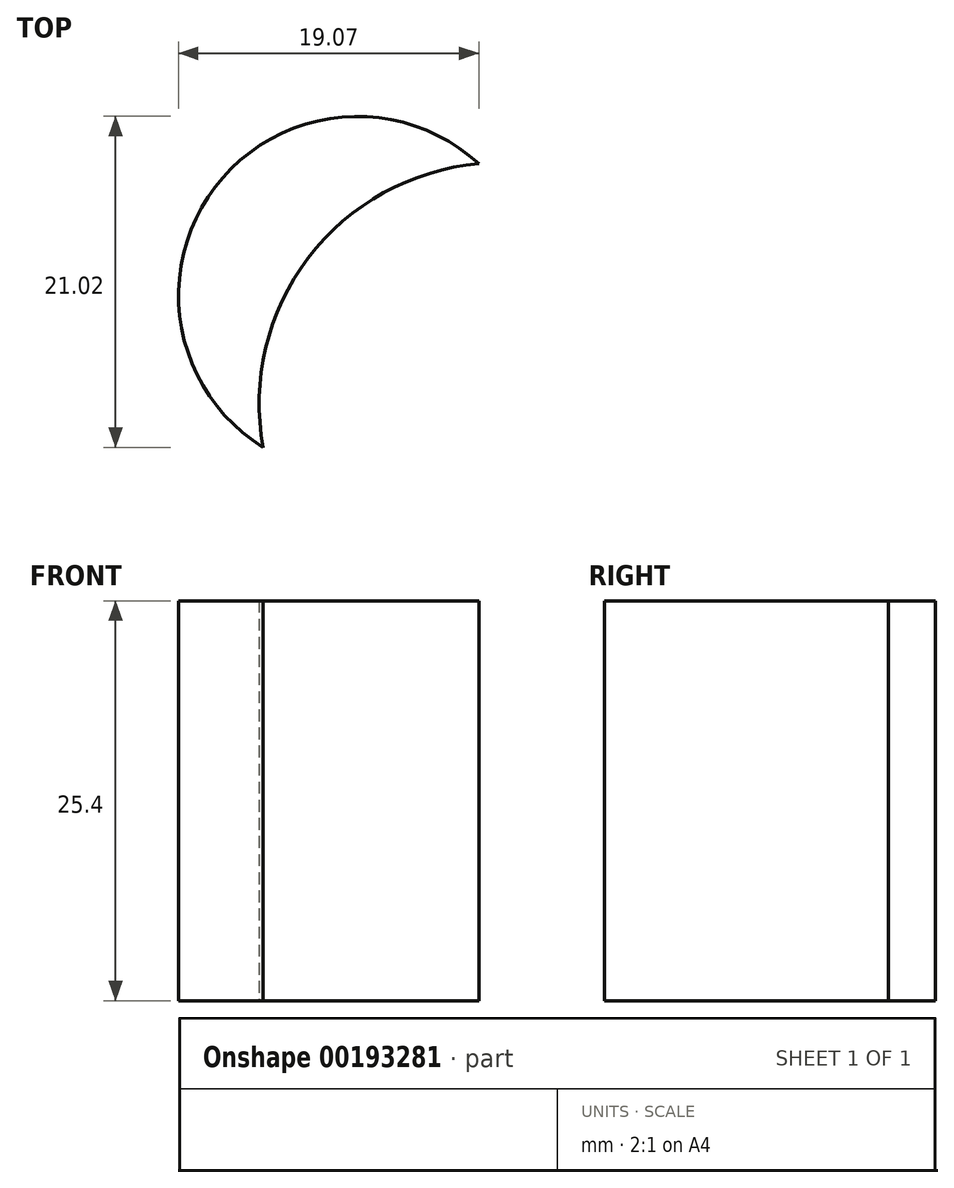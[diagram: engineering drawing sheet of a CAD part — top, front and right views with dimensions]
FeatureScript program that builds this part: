
annotation { "Feature Type Name" : "Feature", "Feature Type Description" : "" }
export const myFeature = defineFeature(function(context is Context, id is Id, definition is map)
    precondition{}
    {
        {
            var Q0;
            Q0=qCreatedBy(makeId("Top.planeOp"),FACE);
            var sketch = newSketch(context, id + "F0", { "sketchPlane" : qUnion([Q0])});
            skLineSegment(sketch, "E0.bottom", {"start": v(0, 38.25) * mm, "end": v(-44.88, 38.25) * mm});
            skLineSegment(sketch, "E0.top", {"start": v(0, 0) * mm, "end": v(-44.88, 0) * mm});
            skLineSegment(sketch, "E0.left", {"start": v(0, 38.25) * mm, "end": v(0, 0) * mm});
            skLineSegment(sketch, "E0.right", {"start": v(-44.88, 38.25) * mm, "end": v(-44.88, 0) * mm});
            skCircle(sketch, "E1", {"center": v(-29.24, 22.95) * mm, "radius": 11.36 * mm});
            skCircle(sketch, "E2", {"center": v(-22.94, 13.5) * mm, "radius": 3.72 * mm});
            skCircle(sketch, "E3", {"center": v(-20.2, 16.07) * mm, "radius": 15.3 * mm});
            skSolve(sketch);
        }
        {
            var Q0;
            {var subQ0=sQuery(id+"F0.wireOp",EDGE,"E3");var subQ1=sQuery(id+"F0.wireOp",EDGE,"E1");var subQ2=makeQuery(id+"F0.imprint","INTERSECT",VERTEX,{"disambiguationData":[OD(0.0)],"derivedFrom":[subQ1,subQ0]});Q0=makeQuery(id+"F0.imprint","IMPRINT",FACE,{"disambiguationData":[TD([[makeQuery(id+"F0.imprint","IMPRINT",EDGE,{"disambiguationData":[TD([[subQ2,-1.0]])],"derivedFrom":subQ1}),1.0]])]});}
            extrude(context, id + "F1", {"entities" : qUnion([Q0]), "depth" : 25.4 * mm});
        }
    });
